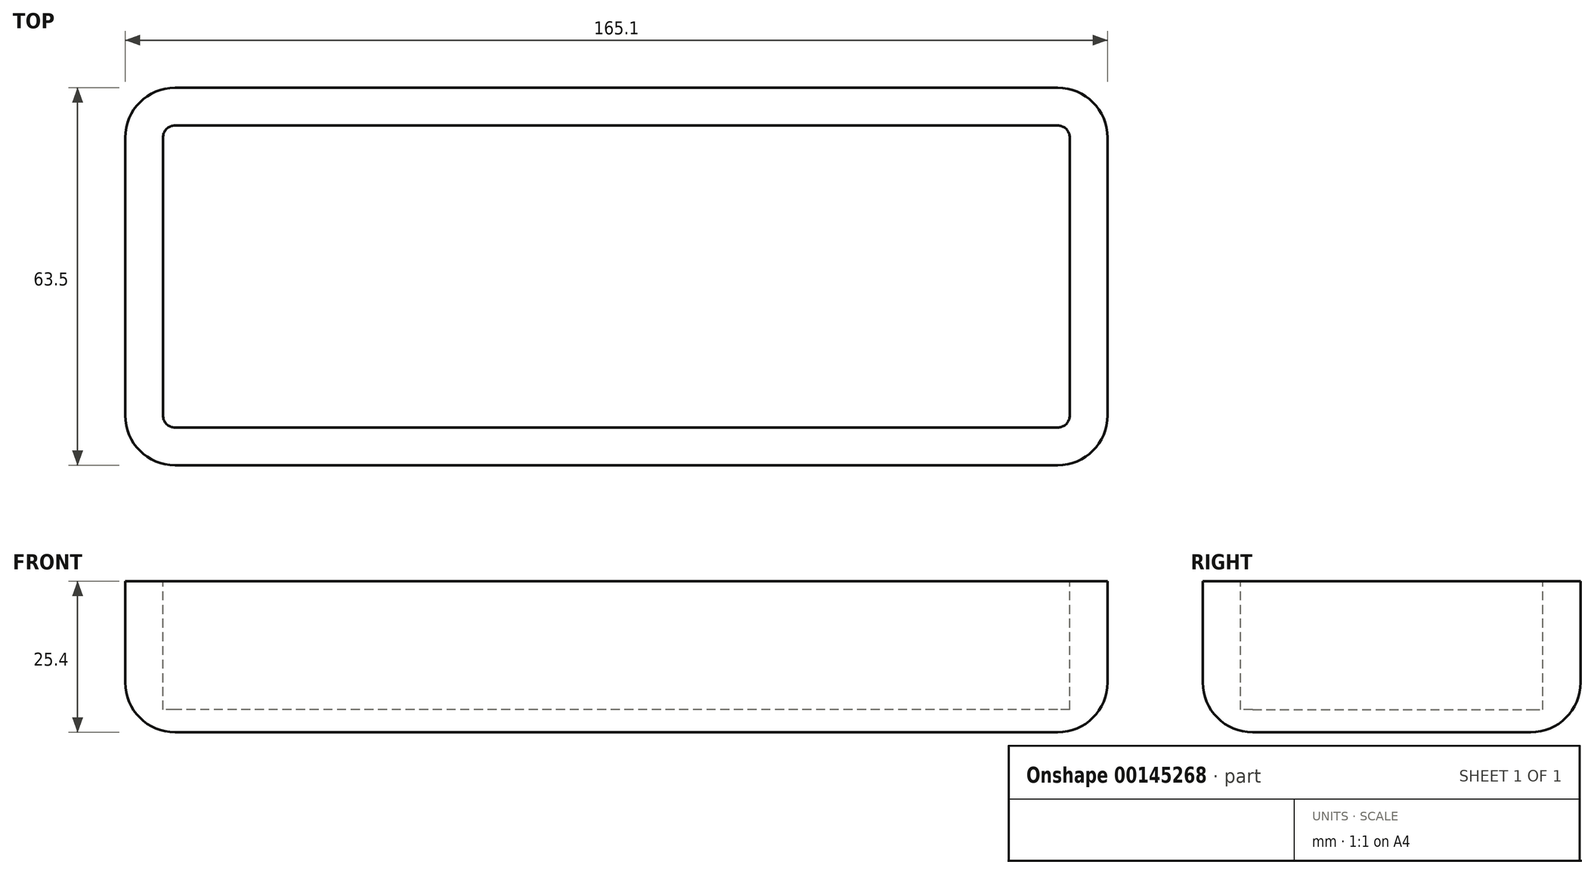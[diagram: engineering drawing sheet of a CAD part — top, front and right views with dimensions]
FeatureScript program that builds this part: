
annotation { "Feature Type Name" : "Feature", "Feature Type Description" : "" }
export const myFeature = defineFeature(function(context is Context, id is Id, definition is map)
    precondition{}
    {
        {
            var Q0;
            Q0=qCreatedBy(makeId("Top.planeOp"),FACE);
            var sketch = newSketch(context, id + "F0", { "sketchPlane" : qUnion([Q0])});
            skLineSegment(sketch, "E0.bottom", {"start": v(-73.52, 45.37) * mm, "end": v(91.58, 45.37) * mm});
            skLineSegment(sketch, "E0.top", {"start": v(-73.52, -18.13) * mm, "end": v(91.58, -18.13) * mm});
            skLineSegment(sketch, "E0.left", {"start": v(-73.52, 45.37) * mm, "end": v(-73.52, -18.13) * mm});
            skLineSegment(sketch, "E0.right", {"start": v(91.58, 45.37) * mm, "end": v(91.58, -18.13) * mm});
            skSolve(sketch);
        }
        {
            var Q0;
            Q0 = qSketchRegion(id + "F0", true);
            extrude(context, id + "F1", {"entities" : qUnion([Q0]), "depth" : 25.4 * mm});
        }
        {
            var Q0;
            Q0=makeQuery(id+"F1.opExtrude","SWEPT_EDGE",EDGE,{"disambiguationData":[OSD([sQuery(id+"F0.wireOp",EDGE,"E0.top"),sQuery(id+"F0.wireOp",EDGE,"E0.right")])]});
            var Q1;
            Q1=makeQuery(id+"F1.opExtrude","SWEPT_EDGE",EDGE,{"disambiguationData":[OSD([sQuery(id+"F0.wireOp",EDGE,"E0.bottom"),sQuery(id+"F0.wireOp",EDGE,"E0.right")])]});
            var Q2;
            Q2=makeQuery(id+"F1.opExtrude","SWEPT_EDGE",EDGE,{"disambiguationData":[OSD([sQuery(id+"F0.wireOp",EDGE,"E0.bottom"),sQuery(id+"F0.wireOp",EDGE,"E0.left")])]});
            var Q3;
            Q3=makeQuery(id+"F1.opExtrude","SWEPT_EDGE",EDGE,{"disambiguationData":[OSD([sQuery(id+"F0.wireOp",EDGE,"E0.top"),sQuery(id+"F0.wireOp",EDGE,"E0.left")])]});
            var Q4;
            Q4=makeQuery(id+"F1.opExtrude","CAP_FACE",FACE,{"disambiguationData":[OSD([sQuery(id+"F0.wireOp",EDGE,"E0.bottom"),sQuery(id+"F0.wireOp",EDGE,"E0.top"),sQuery(id+"F0.wireOp",EDGE,"E0.left"),sQuery(id+"F0.wireOp",EDGE,"E0.right")])],"isStart":true});
            fillet(context, id + "F2", {"entities" : qUnion([Q0, Q1, Q2, Q3, Q4]), "radius" : 8.38 * mm, "tangentPropagation" : true, "allowEdgeOverflow" : false});
        }
        {
            var Q0;
            Q0=makeQuery(id+"F1.opExtrude","CAP_FACE",FACE,{"disambiguationData":[OSD([sQuery(id+"F0.wireOp",EDGE,"E0.bottom"),sQuery(id+"F0.wireOp",EDGE,"E0.top"),sQuery(id+"F0.wireOp",EDGE,"E0.left"),sQuery(id+"F0.wireOp",EDGE,"E0.right")])],"isStart":false});
            var sketch = newSketch(context, id + "F3", { "sketchPlane" : qUnion([Q0])});
            skLineSegment(sketch, "E1.0.0", {"start": v(83.2, 45.37) * mm, "end": v(-65.14, 45.37) * mm});
            skArc(sketch, "E1.0.1", {"start": v(-65.14, 45.37) * mm, "mid": v(-71.07, 42.91) * mm, "end": v(-73.52, 36.99) * mm});
            skLineSegment(sketch, "E1.0.2", {"start": v(-73.52, 36.99) * mm, "end": v(-73.52, -9.75) * mm});
            skArc(sketch, "E1.0.3", {"start": v(-73.52, -9.75) * mm, "mid": v(-71.07, -15.68) * mm, "end": v(-65.14, -18.13) * mm});
            skLineSegment(sketch, "E1.0.4", {"start": v(-65.14, -18.13) * mm, "end": v(83.2, -18.13) * mm});
            skArc(sketch, "E1.0.5", {"start": v(83.2, -18.13) * mm, "mid": v(89.12, -15.68) * mm, "end": v(91.58, -9.75) * mm});
            skLineSegment(sketch, "E1.0.6", {"start": v(91.58, -9.75) * mm, "end": v(91.58, 36.99) * mm});
            skArc(sketch, "E1.0.7", {"start": v(91.58, 36.99) * mm, "mid": v(89.12, 42.91) * mm, "end": v(83.2, 45.37) * mm});
            skArc(sketch, "E2.0", {"start": v(85.23, 36.99) * mm, "mid": v(84.63, 38.42) * mm, "end": v(83.2, 39.02) * mm});
            skLineSegment(sketch, "E2.1", {"start": v(85.23, -9.75) * mm, "end": v(85.23, 36.99) * mm});
            skLineSegment(sketch, "E2.2", {"start": v(83.2, 39.02) * mm, "end": v(-65.14, 39.02) * mm});
            skArc(sketch, "E2.3", {"start": v(83.2, -11.78) * mm, "mid": v(84.63, -11.19) * mm, "end": v(85.23, -9.75) * mm});
            skArc(sketch, "E2.4", {"start": v(-65.14, 39.02) * mm, "mid": v(-66.58, 38.42) * mm, "end": v(-67.17, 36.99) * mm});
            skLineSegment(sketch, "E2.5", {"start": v(-67.17, 36.99) * mm, "end": v(-67.17, -9.75) * mm});
            skArc(sketch, "E2.6", {"start": v(-67.17, -9.75) * mm, "mid": v(-66.58, -11.19) * mm, "end": v(-65.14, -11.78) * mm});
            skLineSegment(sketch, "E2.7", {"start": v(-65.14, -11.78) * mm, "end": v(83.2, -11.78) * mm});
            skSolve(sketch);
        }
        {
            var Q0;
            Q0=makeQuery(id+"F3.imprint","IMPRINT",FACE,{"disambiguationData":[TD([[makeQuery(id+"F3.imprint","IMPRINT",EDGE,{"derivedFrom":sQuery(id+"F3.wireOp",EDGE,"E2.0")}),1.0]])]});
            extrude(context, id + "F4", {"entities" : qUnion([Q0]), "operationType" : NewBodyOperationType.REMOVE, "oppositeDirection" : true, "depth" : 21.59 * mm});
        }
    });
